# Revit family: Wasserzählergarnitur 4126
name_source: partatom
category: Rohrzubehör
revit_build: Autodesk Revit 2018 (Build: 20190510_1515(x64)
units: mm (PartAtom-declared; Revit-internal decimal feet)

## family parameters
Arbeitsebenenbasiert = Nein
Beim Laden mit Abzugskörper schneiden = Nein
Bemaßung runder Anschluss = Durchmesser verwenden
Gemeinsam genutzt = Nein
Immer vertikal = Ja
OmniClass-Nummer = 23.65.55.14
OmniClass-Titel = Valves for Liquid Services
Teiletyp = Unterbricht

## types (1)
- Wasserzählergarnitur 4126
    Anwendungsgebiet = Zum Absperren von Trinkwasserleitungen und zum Einsetzen einer Wasserzählergarnitur.
    Bügel = offenen verzinkten Stahlblech
    Gehäuse = entzinkungsbeständiges Gussmessing CC770S
    Gelegentliche Temperaturanstiege (Ventil) = bis 95°C, nicht länger als eine Stunde
    Handrad = Kunststoff, grün
    Hersteller = HERZ Armaturen Ges.m.b.H.
    Hinweis = Gemäß Art 33 der REACH-Verordnung (EG Nr. 1907/2006) sind wir verpflichtet, darauf hinzuweisen, dass der Stoff Blei auf der SVHC-Liste geführt wird und dass alle aus Messing bestehenden Bauteile, die in unseren Erzeugnissen verarbeitet sind, mehr als 0,1 % (w/w) Blei (CAS: 7439-92-1 / EINECS: 231-100-4) enthalten.
Da Blei als Legierungsbestandteil fest gebunden ist, sind keine Expositionen zu erwarten und daher sind keine zusätzlichen Angaben zur sicheren Verwendung notwendig.
    Kegel = geschmiedetes Messing CW 617N
    L15 = 2 mm  [stored 0.00656168 ft]
    Max. Betriebsdruck (Ventil) = 1600000.0 Pa
    Max. Betriebstemperatur (Ventil) = 80 °C
    Max. Differenzdruck auf geschlossenen Sitz (Ventil) = 1000000.0 Pa
    Medium = Trinkwasser
    R50 = 4 mm  [stored 0.0131234 ft]
    S = 3 mm  [stored 0.00984252 ft]
    S03 = 10 mm  [stored 0.0328084 ft]
    SCTWCODE = 02;01;02
    SCTWSEQ = AW;SBT_TYP_AW="105";2
    SC_NennweiteBerechnet = 0
    Spindel = geschmiedetes Messing CW 617N
    T01 = 3 mm  [stored 0.00984252 ft]
    T02 = 17 mm  [stored 0.0557743 ft]
    URL = www.herz-armaturen.at
    W01 = 20.00°
    Öffnungsdruck des Rückflussverhinderers (Ventil) = gemäß DIN EN 13959

note: [stored X ft] marks values corroborated as IEEE doubles in the binary element streams (Revit-internal decimal feet)
